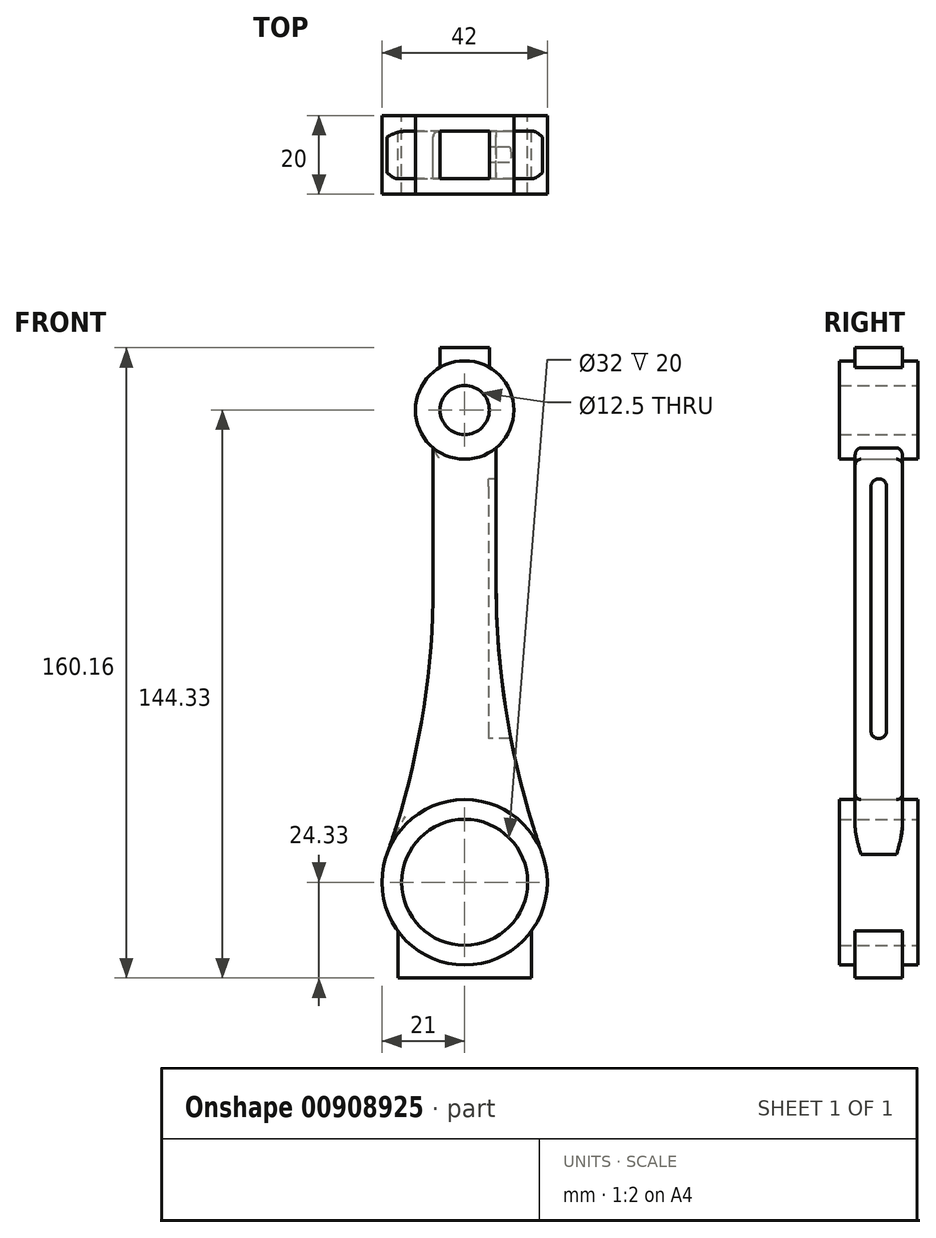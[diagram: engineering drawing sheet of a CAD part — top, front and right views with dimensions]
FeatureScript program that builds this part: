
annotation { "Feature Type Name" : "Feature", "Feature Type Description" : "" }
export const myFeature = defineFeature(function(context is Context, id is Id, definition is map)
    precondition{}
    {
        {
            var Q0;
            Q0=qCreatedBy(makeId("Front.planeOp"),FACE);
            var sketch = newSketch(context, id + "F0", { "sketchPlane" : qUnion([Q0])});
            skCircle(sketch, "E0", {"center": v(0, 0) * mm, "radius": 21 * mm});
            skCircle(sketch, "E1", {"center": v(0, 0) * mm, "radius": 16 * mm});
            skCircle(sketch, "E2", {"center": v(0, 120) * mm, "radius": 12.5 * mm});
            skCircle(sketch, "E3", {"center": v(0, 120) * mm, "radius": 6.25 * mm});
            skSolve(sketch);
        }
        {
            var Q0;
            Q0 = qSketchRegion(id + "F0", true);
            extrude(context, id + "F1", {"entities" : qUnion([Q0]), "endBound" : BoundingType.SYMMETRIC, "depth" : 20 * mm, "offsetDistance" : 25 * mm});
        }
        {
            var Q0;
            Q0=qCreatedBy(makeId("Front.planeOp"),FACE);
            var sketch = newSketch(context, id + "F2", { "sketchPlane" : qUnion([Q0])});
            skArc(sketch, "E4.0", {"start": v(-8, 110.4) * mm, "mid": v(0, 107.5) * mm, "end": v(8, 110.4) * mm});
            skArc(sketch, "E4.1", {"start": v(19.79, 7.03) * mm, "mid": v(0, 21) * mm, "end": v(-19.79, 7.03) * mm});
            skLineSegment(sketch, "E5", {"start": v(8, 110.4) * mm, "end": v(8, 75.4) * mm});
            skLineSegment(sketch, "E6", {"start": v(0, 120) * mm, "end": v(0, 90.03) * mm, "construction": true});
            skArc(sketch, "E7", {"start": v(8, 75.4) * mm, "mid": v(10.97, 40.7) * mm, "end": v(19.79, 7.03) * mm});
            skLineSegment(sketch, "E8.MirrorCS", {"start": v(-8, 110.4) * mm, "end": v(-8, 75.4) * mm});
            skArc(sketch, "E9.MirrorCS", {"start": v(-8, 75.4) * mm, "mid": v(-10.97, 40.7) * mm, "end": v(-19.79, 7.03) * mm});
            skSolve(sketch);
        }
        {
            var Q0;
            Q0 = qSketchRegion(id + "F2", true);
            extrude(context, id + "F3", {"entities" : qUnion([Q0]), "endBound" : BoundingType.SYMMETRIC, "depth" : 12 * mm, "offsetDistance" : 25 * mm});
        }
        {
            var Q0;
            Q0=qCreatedBy(makeId("Front.planeOp"),FACE);
            var sketch = newSketch(context, id + "F4", { "sketchPlane" : qUnion([Q0])});
            skLineSegment(sketch, "E10", {"start": v(0, 139.13) * mm, "end": v(0, -40.3) * mm, "construction": true});
            skArc(sketch, "E11.0", {"start": v(0, 107.5) * mm, "mid": v(12.07, 123.24) * mm, "end": v(-6.25, 130.83) * mm});
            skLineSegment(sketch, "E12", {"start": v(-6.25, 135.83) * mm, "end": v(-6.25, 130.83) * mm});
            skLineSegment(sketch, "E13.MirrorCS", {"start": v(6.25, 135.83) * mm, "end": v(6.25, 130.83) * mm});
            skLineSegment(sketch, "E14", {"start": v(-6.25, 135.83) * mm, "end": v(6.25, 135.83) * mm});
            skArc(sketch, "E15.0", {"start": v(-17, -12.33) * mm, "mid": v(0, -21) * mm, "end": v(17, -12.33) * mm});
            skLineSegment(sketch, "E16", {"start": v(-17, -24.33) * mm, "end": v(-17, -12.33) * mm});
            skLineSegment(sketch, "E17.MirrorCS", {"start": v(17, -24.33) * mm, "end": v(17, -12.33) * mm});
            skLineSegment(sketch, "E18", {"start": v(-17, -24.33) * mm, "end": v(17, -24.33) * mm});
            skSolve(sketch);
        }
        {
            var Q0;
            Q0 = qSketchRegion(id + "F4", true);
            extrude(context, id + "F5", {"entities" : qUnion([Q0]), "operationType" : NewBodyOperationType.ADD, "endBound" : BoundingType.SYMMETRIC, "depth" : 12 * mm, "offsetDistance" : 25 * mm});
        }
        {
            var Q0;
            Q0=makeQuery(id+"F5.opExtrude","SWEPT_EDGE",EDGE,{"disambiguationData":[OSD([sQuery(id+"F4.wireOp",EDGE,"E11.0"),sQuery(id+"F4.wireOp",EDGE,"E13.MirrorCS")])]});
            var Q1;
            Q1=makeQuery(id+"F5.opExtrude","CAP_EDGE",EDGE,{"disambiguationData":[OSD([sQuery(id+"F4.wireOp",EDGE,"E11.0")])],"isStart":false});
            var Q2;
            Q2=makeQuery(id+"F5.opExtrude","CAP_EDGE",EDGE,{"disambiguationData":[OSD([sQuery(id+"F4.wireOp",EDGE,"E11.0")])],"isStart":true});
            var Q3;
            Q3=makeQuery(id+"F5.opExtrude","SWEPT_EDGE",EDGE,{"disambiguationData":[OSD([sQuery(id+"F4.wireOp",EDGE,"E11.0"),sQuery(id+"F4.wireOp",EDGE,"E12")])]});
            var Q4;
            Q4=makeQuery(id+"F3.opExtrude","CAP_EDGE",EDGE,{"disambiguationData":[OSD([sQuery(id+"F2.wireOp",EDGE,"E4.0")])],"isStart":true});
            var Q5;
            Q5=makeQuery(id+"F3.opExtrude","CAP_EDGE",EDGE,{"disambiguationData":[OSD([sQuery(id+"F2.wireOp",EDGE,"E4.1")])],"isStart":true});
            var Q6;
            Q6=makeQuery(id+"F3.opExtrude","CAP_EDGE",EDGE,{"disambiguationData":[OSD([sQuery(id+"F2.wireOp",EDGE,"E4.1")])],"isStart":false});
            var Q7;
            Q7=makeQuery(id+"F3.opExtrude","CAP_EDGE",EDGE,{"disambiguationData":[OSD([sQuery(id+"F2.wireOp",EDGE,"E9.MirrorCS")])],"isStart":true});
            var Q8;
            Q8=makeQuery(id+"F3.opExtrude","CAP_EDGE",EDGE,{"disambiguationData":[OSD([sQuery(id+"F2.wireOp",EDGE,"E4.0")])],"isStart":false});
            var Q9;
            Q9=makeQuery(id+"F5.opExtrude","SWEPT_EDGE",EDGE,{"disambiguationData":[OSD([sQuery(id+"F4.wireOp",EDGE,"E15.0"),sQuery(id+"F4.wireOp",EDGE,"E16")])]});
            var Q10;
            Q10=makeQuery(id+"F5.opExtrude","CAP_EDGE",EDGE,{"disambiguationData":[OSD([sQuery(id+"F4.wireOp",EDGE,"E15.0")])],"isStart":false});
            var Q11;
            Q11=makeQuery(id+"F5.opExtrude","CAP_EDGE",EDGE,{"disambiguationData":[OSD([sQuery(id+"F4.wireOp",EDGE,"E15.0")])],"isStart":true});
            var Q12;
            Q12=makeQuery(id+"F5.opExtrude","SWEPT_EDGE",EDGE,{"disambiguationData":[OSD([sQuery(id+"F4.wireOp",EDGE,"E15.0"),sQuery(id+"F4.wireOp",EDGE,"E17.MirrorCS")])]});
            fillet(context, id + "F6", {"entities" : qUnion([Q0, Q1, Q2, Q3, Q4, Q5, Q6, Q7, Q8, Q9, Q10, Q11, Q12]), "radius" : 1.5 * mm, "tangentPropagation" : true, "allowEdgeOverflow" : false});
        }
        {
            var Q0;
            Q0=qCreatedBy(makeId("Right.planeOp"),FACE);
            cPlane(context, id + "F7", {"entities" : qUnion([Q0]), "cplaneType" : CPlaneType.OFFSET, "offset" : 6 * mm, "width" : 150 * mm, "height" : 150 * mm});
        }
        {
            var Q0;
            Q0=qCreatedBy(id+"F7.planeOp",FACE);
            var sketch = newSketch(context, id + "F8", { "sketchPlane" : qUnion([Q0])});
            skLineSegment(sketch, "E19", {"start": v(0, 100.5) * mm, "end": v(0, 38.5) * mm});
            skArc(sketch, "E20.0.startCap", {"start": v(-2, 100.5) * mm, "mid": v(0, 102.5) * mm, "end": v(2, 100.5) * mm});
            skArc(sketch, "E20.0.endCap", {"start": v(2, 38.5) * mm, "mid": v(0, 36.5) * mm, "end": v(-2, 38.5) * mm});
            skLineSegment(sketch, "E20.0.left", {"start": v(2, 100.5) * mm, "end": v(2, 38.5) * mm});
            skLineSegment(sketch, "E20.0.right", {"start": v(-2, 100.5) * mm, "end": v(-2, 38.5) * mm});
            skLineSegment(sketch, "E21", {"start": v(-14.56, 120.5) * mm, "end": v(11.54, 120.5) * mm, "construction": true});
            skSolve(sketch);
        }
        {
            var Q0;
            Q0 = qSketchRegion(id + "F8", true);
            extrude(context, id + "F9", {"entities" : qUnion([Q0]), "operationType" : NewBodyOperationType.REMOVE, "depth" : 12 * mm, "offsetDistance" : 25 * mm});
        }
    });
